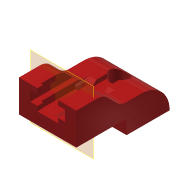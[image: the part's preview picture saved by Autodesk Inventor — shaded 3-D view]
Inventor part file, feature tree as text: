
AUTODESK INVENTOR PART (.ipt)
format: ipt  version: 2021 (Build 250183000, 183)  size: 638,464 bytes
history: native  units: mm
features: sketch x34, extrude x28, projected_geometry x19, chamfer x10, fillet x8, reference x8, plane x4, mirror x3, revolve x2, other x2, hole x1
ambient origin geometry x8: Origin, YZ Plane, XZ Plane, XY Plane, X Axis, Y Axis, Z Axis, Center Point
bodies: Volumenkörper1 (feature_tree)
feature tree (119):
  extrude  "Extrusion1"  Depth=15.0mm
  extrude  "Extrusion2"  Depth=5.8mm
  extrude  "Extrusion3"  Depth=20.0mm
  hole  "Bohrung1"  [1 undecoded]
  fillet  "Rundung1"  Radius=10.0mm
  sketch  "Skizze5"  dims[d11=3.5mm d12=6.0mm d13=6.0mm d14=5.0mm d15=90.0deg d16=90.0mm d17=0.0mm d18=10.0mm]
  sketch  "Skizze6"  dims[d19=11.5mm]
  plane  "Arbeitsebene1"
  revolve  "Umdrehung1"
  sketch  "Skizze8"  dims[d21=5.375mm]
  plane  "Arbeitsebene2"
  revolve  "Umdrehung2"
  chamfer  "Fase1"  Distance=2.0mm Angle=45.0deg
  chamfer  "Fase2"  Distance=2.0mm Angle=45.0deg
  extrude  "Extrusion4"  Depth=12.5mm
  chamfer  "Fase6"  Distance=1.5mm
  plane  "Arbeitsebene4"
  extrude  "Extrusion8"  Depth=2.0mm TaperAngle=0.0deg
  plane  "Arbeitsebene3"
  extrude  "Extrusion10"  Depth=3.5mm TaperAngle=0.0deg
  extrude  "Extrusion11"  Depth=10.0mm
  fillet  "Rundung12"  Radius=10.0mm
  sketch  "Skizze19"  dims[d33=12.5mm d34=30.0mm d35=1.5mm d36=0.0mm]
  extrude  "Extrusion12"  Depth=8.7mm
  extrude  "Extrusion13"  Depth=10.0mm TaperAngle=0.0deg
  extrude  "Extrusion14"  Depth=2.0mm
  chamfer  "Fase8"  Distance=0.65mm
  chamfer  "Fase9"  Distance=2.0mm Angle=45.0deg
  extrude  "Extrusion15"  Depth=2.0mm TaperAngle=0.0deg
  extrude  "Extrusion16"  Depth=0.65mm TaperAngle=0.0deg
  extrude  "Extrusion17"  Depth=2.0mm TaperAngle=0.0deg
  chamfer  "Fase11"  Distance=0.6mm
  extrude  "Extrusion18"  Depth=1.44mm
  extrude  "Extrusion19"  TaperAngle=0.0deg  [1 undecoded]
  extrude  "Extrusion20"  Depth=2.0mm
  extrude  "Extrusion21"  Depth=2.0mm TaperAngle=0.0deg
  chamfer  "Fase12"  Distance=0.8mm
  fillet  "Rundung15"  Radius=0.8mm
  chamfer  "Fase13"  Distance=13.65mm
  extrude  "Extrusion22"  Depth=0.785mm
  extrude  "Extrusion23"  TaperAngle=0.0deg  [1 undecoded]
  mirror  "Spiegeln1"
  extrude  "Extrusion24"  Depth=2.0mm TaperAngle=45.0deg
  extrude  "Extrusion25"  Depth=2.0mm
  extrude  "Extrusion26"  Depth=2.0mm TaperAngle=0.0deg
  mirror  "Spiegeln2"
  extrude  "Extrusion27"  TaperAngle=0.0deg  [1 undecoded]
  extrude  "Extrusion28"  TaperAngle=0.0deg  [1 undecoded]
  chamfer  "Fase14"  Distance=5.0mm
  fillet  "Rundung16"  Radius=1.0mm
  extrude  "Extrusion29"  Depth=2.0mm
  mirror  "Spiegeln3"
  extrude  "Extrusion30"  Depth=2.0mm
  extrude  "Extrusion31"  Depth=2.0mm
  fillet  "Rundung17"  [1 undecoded]
  fillet  "Rundung18"  Radius=2.0mm
  fillet  "Rundung19"  Radius=2.0mm
  extrude  "Extrusion32"  [1 undecoded]
  chamfer  "Fase15"  [1 undecoded]
  fillet  "Rundung20"  [1 undecoded]
  sketch  "Skizze1"  dims[d0=20.0mm d1=15.0mm]
  sketch  "Skizze2"  dims[d2=5.0mm d3=0.0mm d4=5.8mm]
  sketch  "Skizze3"  dims[d5=1.0mm d6=0.0mm d7=20.0mm]
  sketch  "Skizze4"  dims[d8=30.5mm d9=5.0mm d10=0.0mm]
  projected_geometry  "Projizierte Kontur1"
  sketch  "Skizze7"  dims[d20=5.375mm]
  sketch  "Skizze9"  dims[d22=3.0mm]
  sketch  "Skizze10"  dims[d23=9.75mm]
  sketch  "Skizze15"  dims[d24=90.0deg]
  sketch  "Skizze17"  dims[d25=25.75mm]
  sketch  "Skizze18"  dims[d26=90.0deg d27=1.0mm d28=2.0mm d29=45.0deg d30=1.0mm d31=2.0mm d32=45.0deg]
  sketch  "Skizze20"  dims[d68=1.0mm d69=2.0mm d70=45.0deg d71=18.0mm d72=0.0mm]
  projected_geometry  "Projizierte Kontur7"
  sketch  "Skizze21"  dims[d85=11.26mm d86=3.5mm d87=0.0mm]
  projected_geometry  "Projizierte Kontur8"
  sketch  "Skizze22"  dims[d88=9.0mm d89=2.4mm d90=10.0mm d91=0.0mm]
  reference  "Referenz3"
  projected_geometry  "Projizierte Kontur9"
  projected_geometry  "Projizierte Kontur10"
  projected_geometry  "Projizierte Kontur11"
  sketch  "Skizze23"  dims[d92=1.0mm d95=8.7mm]
  projected_geometry  "Projizierte Kontur12"
  projected_geometry  "Projizierte Kontur13"
  sketch  "Skizze25"  dims[d96=10.0mm d97=0.0mm d98=1.5mm d99=0.0mm]
  projected_geometry  "Projizierte Kontur15"
  sketch  "Skizze26"  dims[d100=8.5mm d101=3.1mm d102=0.65mm d103=0.0mm d104=0.65mm d105=2.0mm d106=45.0deg]
  sketch  "Skizze27"  dims[d107=0.65mm d108=2.0mm d109=45.0deg d113=6.8mm d114=0.0mm]
  reference  "Referenz4"
  sketch  "Skizze28"  dims[d115=0.8mm d116=0.0mm d117=0.65mm d118=0.0mm]
  sketch  "Skizze29"  dims[d119=0.65mm d120=2.0mm d121=45.0deg d122=0.6mm d123=0.0mm]
  reference  "Referenz5"
  reference  "Referenz6"
  reference  "Referenz7"
  reference  "Referenz8"
  sketch  "Skizze30"  dims[d124=12.5mm d125=0.6mm d126=0.0mm]
  projected_geometry  "Projizierte Kontur16"
  sketch  "Skizze31"  dims[d127=0.6mm d128=0.0mm d129=1.44mm]
  reference  "Referenz9"
  projected_geometry  "Projizierte Kontur17"
  sketch  "Skizze32"  dims[d130=2.68mm d131=0.0mm d132=0.0mm]
  projected_geometry  "Projizierte Kontur18"
  projected_geometry  "Projizierte Kontur19"
  sketch  "Skizze33"  dims[d133=1.0mm d134=2.0mm d135=45.0deg d136=0.2mm]
  sketch  "Skizze34"  dims[d137=0.34mm d138=2.0mm d139=45.0deg d140=0.6mm d141=0.0mm]
  reference  "Referenz25"
  projected_geometry  "Projizierte Kontur20"
  projected_geometry  "Projizierte Kontur21"
  sketch  "Skizze35"  dims[d142=5.0mm d143=0.8mm d144=0.0mm d145=0.8mm d146=0.0mm]
  projected_geometry  "Projizierte Kontur22"
  sketch  "Skizze36"  dims[d147=3.68mm]
  projected_geometry  "Projizierte Kontur23"
  projected_geometry  "Projizierte Kontur24"
  sketch  "Skizze37"  dims[d148=2.55mm]
  projected_geometry  "Projizierte Kontur25"
  sketch  "Skizze38"  dims[d149=4.15mm d150=13.65mm d151=0.0mm]
  sketch  "Skizze39"  dims[d152=0.0mm d153=0.0mm d154=0.785mm]
  sketch  "Skizze40"  dims[d155=0.0mm d156=0.0mm d157=0.0mm d158=0.0mm d159=6.0mm d160=2.0mm d161=45.0deg d162=5.0mm d163=13.65mm d164=0.0mm d165=0.0mm d166=0.0mm d167=0.0mm d168=0.0mm d169=5.0mm d170=1.0mm d171=0.5mm d172=2.35mm d173=2.35mm d174=0.0mm d175=0.0mm d176=1.5mm d177=2.0mm d178=45.0deg d179=2.0mm]
  other  "<userpath>\Desktop\Voron-2-2.4r1\Custom\AB_Connector_Plug_V2_Microfit_Preview.ipt.iam"
  other  "AB_Connector_Plug_V2_Microfit_Preview.ipt.iam"
note: 9 required parameter values undecoded (feature->parameter linkage not recoverable at this tier; creation-order binding heuristic only, values carry confidence <= 0.55)
